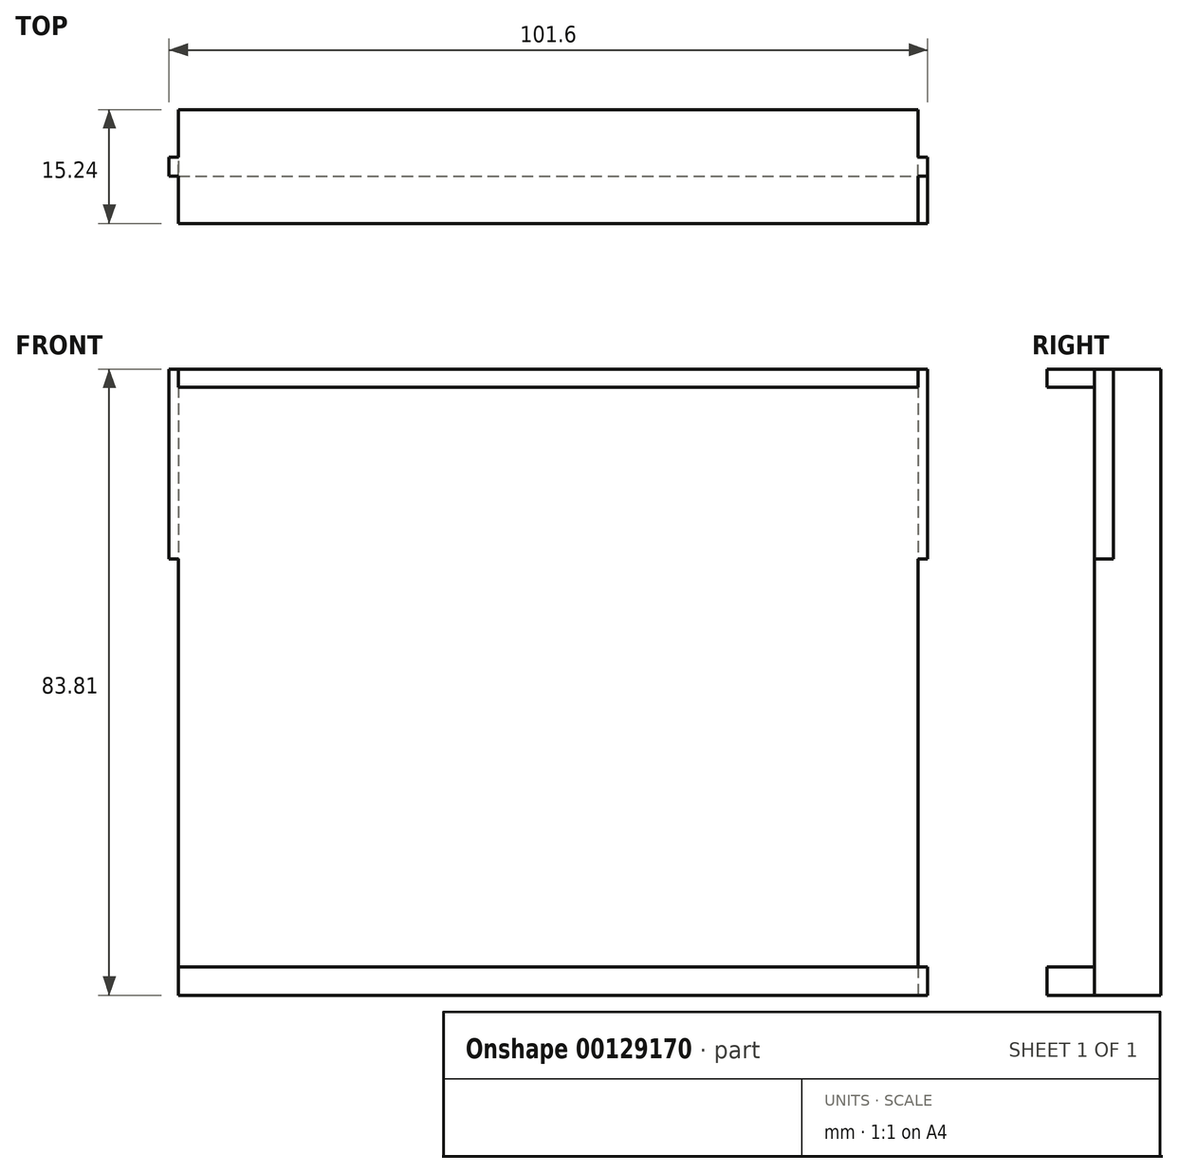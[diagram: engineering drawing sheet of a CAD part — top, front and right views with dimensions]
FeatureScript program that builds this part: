
annotation { "Feature Type Name" : "Feature", "Feature Type Description" : "" }
export const myFeature = defineFeature(function(context is Context, id is Id, definition is map)
    precondition{}
    {
        {
            var Q0;
            Q0=qCreatedBy(makeId("Front.planeOp"),FACE);
            var sketch = newSketch(context, id + "F0", { "sketchPlane" : qUnion([Q0])});
            skLineSegment(sketch, "E0.bottom", {"start": v(-49.53, 40) * mm, "end": v(49.53, 40) * mm});
            skLineSegment(sketch, "E0.top", {"start": v(-49.53, -40) * mm, "end": v(49.53, -40) * mm});
            skLineSegment(sketch, "E0.left", {"start": v(-49.53, 40) * mm, "end": v(-49.53, -40) * mm});
            skLineSegment(sketch, "E0.right", {"start": v(49.53, 40) * mm, "end": v(49.53, -40) * mm});
            skPoint(sketch, "E0.middle", {"position": v(0, 0) * mm});
            skSolve(sketch);
        }
        {
            var Q0;
            Q0=makeQuery(id+"F0.imprint","IMPRINT",FACE,{"disambiguationData":[TD([[makeQuery(id+"F0.imprint","IMPRINT",EDGE,{"derivedFrom":sQuery(id+"F0.wireOp",EDGE,"E0.bottom")}),-1.0]])]});
            extrude(context, id + "F1", {"entities" : qUnion([Q0]), "depth" : 8.9 * mm});
        }
        {
            var Q0;
            Q0=makeQuery(id+"F1.opExtrude","SWEPT_FACE",FACE,{"disambiguationData":[OSD([sQuery(id+"F0.wireOp",EDGE,"E0.right")])]});
            var sketch = newSketch(context, id + "F2", { "sketchPlane" : qUnion([Q0])});
            skLineSegment(sketch, "E1.bottom", {"start": v(-8.9, 40) * mm, "end": v(-6.35, 40) * mm});
            skLineSegment(sketch, "E1.top", {"start": v(-8.89, 14.6) * mm, "end": v(-6.35, 14.6) * mm});
            skLineSegment(sketch, "E1.left", {"start": v(-8.9, 40) * mm, "end": v(-8.9, 14.6) * mm});
            skLineSegment(sketch, "E1.right", {"start": v(-6.35, 40) * mm, "end": v(-6.35, 14.6) * mm});
            skSolve(sketch);
        }
        {
            var Q0;
            Q0=makeQuery(id+"F1.opExtrude","SWEPT_FACE",FACE,{"disambiguationData":[OSD([sQuery(id+"F0.wireOp",EDGE,"E0.left")])]});
            var sketch = newSketch(context, id + "F3", { "sketchPlane" : qUnion([Q0])});
            skLineSegment(sketch, "E2.bottom", {"start": v(8.9, 40) * mm, "end": v(6.35, 40) * mm});
            skLineSegment(sketch, "E2.top", {"start": v(8.9, 14.6) * mm, "end": v(6.35, 14.6) * mm});
            skLineSegment(sketch, "E2.left", {"start": v(8.9, 40) * mm, "end": v(8.9, 14.6) * mm});
            skLineSegment(sketch, "E2.right", {"start": v(6.35, 40) * mm, "end": v(6.35, 14.6) * mm});
            skSolve(sketch);
        }
        {
            var Q0;
            Q0=makeQuery(id+"F3.imprint","IMPRINT",FACE,{"disambiguationData":[TD([[makeQuery(id+"F3.imprint","IMPRINT",EDGE,{"derivedFrom":sQuery(id+"F3.wireOp",EDGE,"E2.bottom")}),1.0]])]});
            extrude(context, id + "F4", {"entities" : qUnion([Q0]), "operationType" : NewBodyOperationType.ADD, "depth" : 1.27 * mm});
        }
        {
            var Q0;
            Q0=makeQuery(id+"F2.imprint","IMPRINT",FACE,{"disambiguationData":[TD([[makeQuery(id+"F2.imprint","IMPRINT",EDGE,{"derivedFrom":sQuery(id+"F2.wireOp",EDGE,"E1.bottom")}),-1.0]])]});
            extrude(context, id + "F5", {"entities" : qUnion([Q0]), "operationType" : NewBodyOperationType.ADD, "depth" : 1.27 * mm});
        }
        {
            var Q0;
            Q0=makeQuery(id+"F1.opExtrude","SWEPT_FACE",FACE,{"disambiguationData":[OSD([sQuery(id+"F0.wireOp",EDGE,"E0.top")])]});
            var sketch = newSketch(context, id + "F6", { "sketchPlane" : qUnion([Q0])});
            skLineSegment(sketch, "E3.bottom", {"start": v(-49.53, 8.9) * mm, "end": v(35.56, 8.9) * mm});
            skLineSegment(sketch, "E4", {"start": v(-49.53, 8.9) * mm, "end": v(-49.53, 15.24) * mm});
            skLineSegment(sketch, "E5", {"start": v(-49.53, 15.24) * mm, "end": v(35.56, 15.24) * mm});
            skLineSegment(sketch, "E6", {"start": v(35.56, 15.24) * mm, "end": v(35.56, 8.9) * mm});
            skSolve(sketch);
        }
        {
            var Q0;
            {var subQ0=sQuery(id+"F6.wireOp",EDGE,"E3.top");Q0=makeQuery(id+"F6.imprint","IMPRINT",FACE,{"disambiguationData":[TD([[makeQuery(id+"F6.imprint","IMPRINT",EDGE,{"derivedFrom":subQ0}),1.0]])]});}
            var Q1;
            Q1=makeQuery(id+"F6.imprint","IMPRINT",FACE,{"disambiguationData":[TD([[makeQuery(id+"F6.imprint","IMPRINT",EDGE,{"derivedFrom":sQuery(id+"F6.wireOp",EDGE,"E3.bottom")}),1.0]])]});
            var Q2;
            Q2=makeQuery(id+"F6.imprint","IMPRINT",FACE,{"disambiguationData":[TD([[makeQuery(id+"F6.imprint","IMPRINT",EDGE,{"derivedFrom":sQuery(id+"F6.wireOp",EDGE,"E3.bottom")}),-1.0]])]});
            extrude(context, id + "F7", {"entities" : qUnion([Q0, Q1, Q2]), "operationType" : NewBodyOperationType.ADD, "depth" : 3.8 * mm});
        }
        {
            var Q0;
            Q0=makeQuery(id+"F5.boolean.opBoolean","MERGE",FACE,{"derivedFrom":[makeQuery(id+"F4.boolean.opBoolean","MERGE",FACE,{"derivedFrom":[makeQuery(id+"F1.opExtrude","CAP_FACE",FACE,{"disambiguationData":[OSD([sQuery(id+"F0.wireOp",EDGE,"E0.bottom"),sQuery(id+"F0.wireOp",EDGE,"E0.top"),sQuery(id+"F0.wireOp",EDGE,"E0.left"),sQuery(id+"F0.wireOp",EDGE,"E0.right")])],"isStart":false}),makeQuery(id+"F4.opExtrude","SWEPT_FACE",FACE,{"disambiguationData":[OSD([sQuery(id+"F3.wireOp",EDGE,"E2.left")])]})]}),makeQuery(id+"F5.opExtrude","SWEPT_FACE",FACE,{"disambiguationData":[OSD([sQuery(id+"F2.wireOp",EDGE,"E1.left")])]})]});
            var sketch = newSketch(context, id + "F8", { "sketchPlane" : qUnion([Q0])});
            skLineSegment(sketch, "E7.bottom", {"start": v(-49.53, 40) * mm, "end": v(49.53, 40) * mm});
            skLineSegment(sketch, "E7.top", {"start": v(-49.53, 37.6) * mm, "end": v(49.53, 37.6) * mm});
            skLineSegment(sketch, "E7.left", {"start": v(-49.53, 40) * mm, "end": v(-49.53, 37.6) * mm});
            skLineSegment(sketch, "E7.right", {"start": v(49.53, 40) * mm, "end": v(49.53, 37.6) * mm});
            skSolve(sketch);
        }
        {
            var Q0;
            Q0=makeQuery(id+"F8.imprint","IMPRINT",FACE,{"disambiguationData":[TD([[makeQuery(id+"F8.imprint","IMPRINT",EDGE,{"derivedFrom":sQuery(id+"F8.wireOp",EDGE,"E7.bottom")}),-1.0]])]});
            extrude(context, id + "F9", {"entities" : qUnion([Q0]), "operationType" : NewBodyOperationType.ADD, "depth" : 6.35 * mm});
        }
        {
            var Q0;
            Q0=makeQuery(id+"F7.opExtrude","SWEPT_FACE",FACE,{"disambiguationData":[OSD([sQuery(id+"F6.wireOp",EDGE,"E6")])]});
            extrude(context, id + "F10", {"entities" : qUnion([Q0]), "operationType" : NewBodyOperationType.ADD, "depth" : 15.24 * mm});
        }
    });
